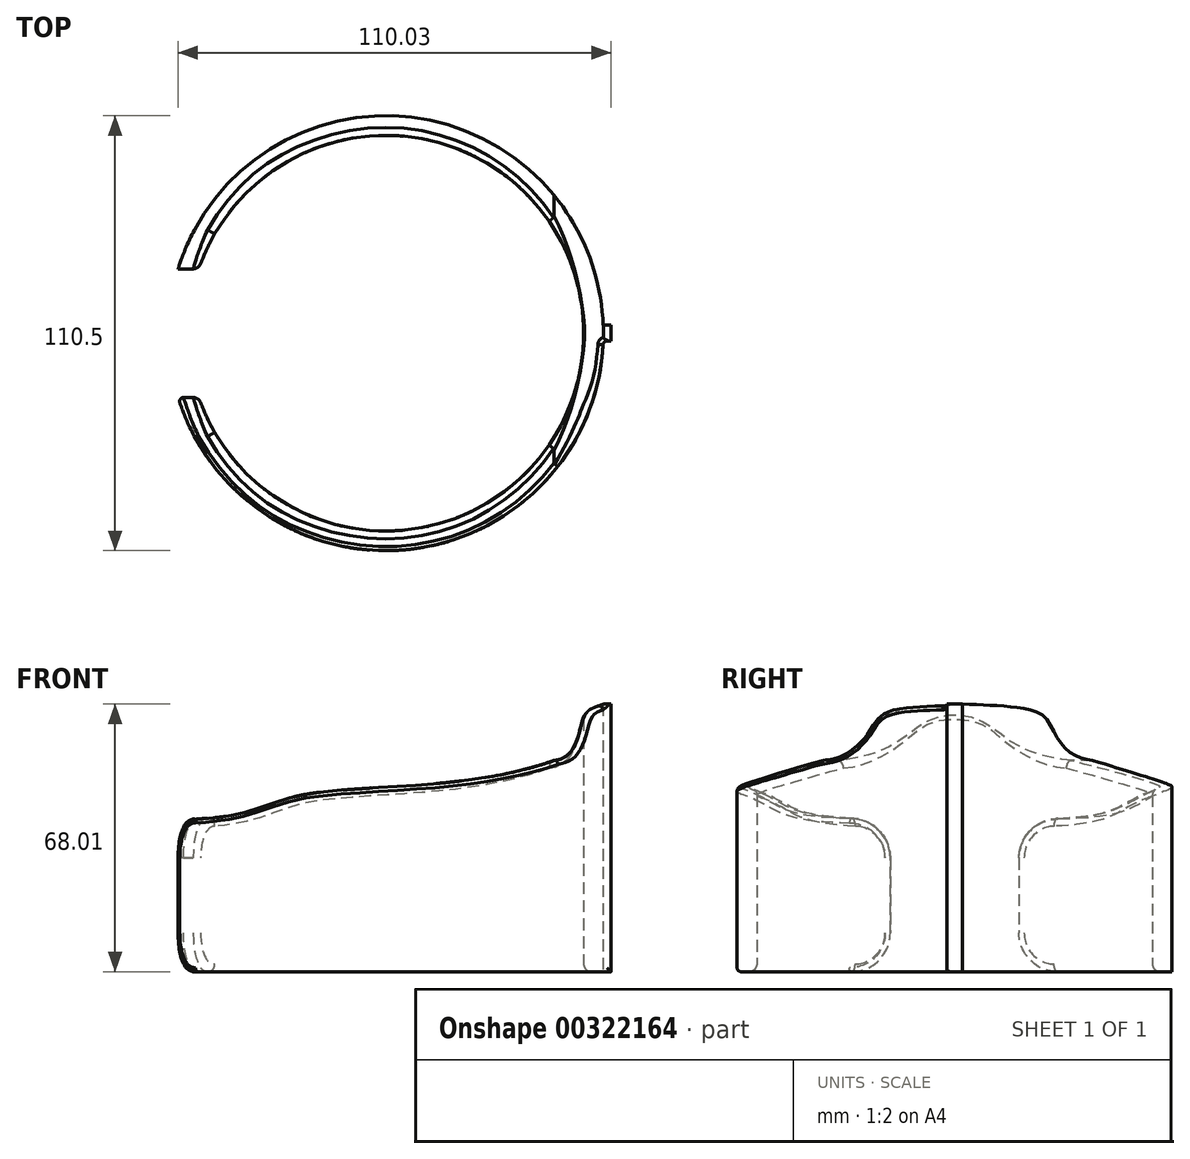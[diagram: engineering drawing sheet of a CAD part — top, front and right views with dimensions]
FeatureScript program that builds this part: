
annotation { "Feature Type Name" : "Feature", "Feature Type Description" : "" }
export const myFeature = defineFeature(function(context is Context, id is Id, definition is map)
    precondition{}
    {
        {
            var Q0;
            Q0=qCreatedBy(makeId("Top.planeOp"),FACE);
            var sketch = newSketch(context, id + "F0", { "sketchPlane" : qUnion([Q0])});
            skArc(sketch, "E0", {"start": v(-52.78, -16.35) * mm, "mid": v(7.28, -54.77) * mm, "end": v(55.21, -2) * mm});
            skArc(sketch, "E1.0", {"start": v(-47.52, -16.35) * mm, "mid": v(50.25, 0) * mm, "end": v(-47.52, 16.35) * mm});
            skLineSegment(sketch, "E2.bottom", {"start": v(-47.52, 16.35) * mm, "end": v(-52.78, 16.35) * mm});
            skLineSegment(sketch, "E2.top", {"start": v(-47.52, -16.35) * mm, "end": v(-52.78, -16.35) * mm});
            skPoint(sketch, "E2.middle", {"position": v(-55.25, 0) * mm});
            skPoint(sketch, "E2.right.start.orphan", {"position": v(-71.6, 16.35) * mm});
            skPoint(sketch, "E3.orphan", {"position": v(-71.6, -16.35) * mm});
            skPoint(sketch, "E4.orphan", {"position": v(-38.9, -16.35) * mm});
            skPoint(sketch, "E5.orphan", {"position": v(-38.9, 16.35) * mm});
            skLineSegment(sketch, "E6", {"start": v(0, 0) * mm, "end": v(55.25, 0) * mm, "construction": true});
            skPoint(sketch, "E7.end.orphan", {"position": v(57.25, 0) * mm});
            skLineSegment(sketch, "E8.bottom", {"start": v(57.25, 2) * mm, "end": v(55.21, 2) * mm});
            skLineSegment(sketch, "E8.top", {"start": v(57.25, -2) * mm, "end": v(55.21, -2) * mm});
            skLineSegment(sketch, "E8.left", {"start": v(57.25, 2) * mm, "end": v(57.25, -2) * mm});
            skPoint(sketch, "E8.middle", {"position": v(55.25, 0) * mm});
            skPoint(sketch, "E9.orphan", {"position": v(53.25, 2) * mm});
            skPoint(sketch, "E10.orphan", {"position": v(53.25, -2) * mm});
            skArc(sketch, "E11.trimOffspring", {"start": v(55.21, 2) * mm, "mid": v(7.28, 54.77) * mm, "end": v(-52.78, 16.35) * mm});
            skSolve(sketch);
        }
        {
            var Q0;
            Q0 = qSketchRegion(id + "F0", true);
            extrude(context, id + "F1", {"entities" : qUnion([Q0]), "depth" : 70 * mm});
        }
        {
            var Q0;
            Q0=qCreatedBy(makeId("Front.planeOp"),FACE);
            cPlane(context, id + "F2", {"entities" : qUnion([Q0]), "cplaneType" : CPlaneType.OFFSET, "offset" : 59 * mm, "width" : 150 * mm, "height" : 150 * mm});
        }
        {
            var Q0;
            Q0=qCreatedBy(id+"F2.planeOp",FACE);
            var sketch = newSketch(context, id + "F3", { "sketchPlane" : qUnion([Q0])});
            skFitSpline(sketch, "E12", {"points": [v(55.25, 68) * mm, v(50.35, 64.85) * mm, v(42.72, 53.7) * mm], "startDerivative": vector(-16.92, -6.6) * mm, "endDerivative": vector(-31.04, -3) * mm});
            skLineSegment(sketch, "E13", {"start": v(42.72, 53.7) * mm, "end": v(42.72, 0) * mm, "construction": true});
            skFitSpline(sketch, "E14", {"points": [v(42.72, 53.7) * mm, v(-21.35, 44.9) * mm, v(-52.78, 38.8) * mm], "startDerivative": vector(-110.2, -40.04) * mm, "endDerivative": vector(-131.82, 1.76) * mm});
            skLineSegment(sketch, "E15.0", {"start": v(-52.78, 70) * mm, "end": v(-52.78, 38.8) * mm});
            skLineSegment(sketch, "E16.0", {"start": v(-52.78, 70) * mm, "end": v(55.21, 70) * mm});
            skPoint(sketch, "E17.start.orphan", {"position": v(-52.78, 0) * mm});
            skPoint(sketch, "E18.start.orphan", {"position": v(55.25, 0) * mm});
            skLineSegment(sketch, "E19.0", {"start": v(57.25, 70) * mm, "end": v(57.25, 0) * mm});
            skLineSegment(sketch, "E20", {"start": v(55.25, 0) * mm, "end": v(55.25, 16.8) * mm});
            skLineSegment(sketch, "E21", {"start": v(55.25, 16.8) * mm, "end": v(57.25, 16.8) * mm});
            skLineSegment(sketch, "E22", {"start": v(57.25, 16.8) * mm, "end": v(57.25, 68) * mm});
            skLineSegment(sketch, "E23", {"start": v(57.25, 68) * mm, "end": v(55.25, 68) * mm});
            skLineSegment(sketch, "E24", {"start": v(55.21, 70) * mm, "end": v(57.25, 70) * mm});
            skSolve(sketch);
        }
        {
            var Q0;
            Q0=makeQuery(id+"F3.imprint","IMPRINT",FACE,{"disambiguationData":[TD([[makeQuery(id+"F3.imprint","IMPRINT",EDGE,{"derivedFrom":sQuery(id+"F3.wireOp",EDGE,"E12")}),-1.0]])]});
            extrude(context, id + "F4", {"entities" : qUnion([Q0]), "operationType" : NewBodyOperationType.REMOVE, "oppositeDirection" : true, "depth" : 127.5 * mm});
        }
        {
            var Q0;
            Q0=makeQuery(id+"F4.boolean.opBoolean","INTERSECT",EDGE,{"derivedFrom":[makeQuery(id+"F1.opExtrude","SWEPT_FACE",FACE,{"disambiguationData":[OSD([sQuery(id+"F0.wireOp",EDGE,"E2.bottom")])]}),makeQuery(id+"F4.opExtrude","SWEPT_FACE",FACE,{"disambiguationData":[OSD([sQuery(id+"F3.wireOp",EDGE,"E14")])]})]});
            var Q1;
            Q1=makeQuery(id+"F4.boolean.opBoolean","INTERSECT",EDGE,{"derivedFrom":[makeQuery(id+"F1.opExtrude","SWEPT_FACE",FACE,{"disambiguationData":[OSD([sQuery(id+"F0.wireOp",EDGE,"E2.top")])]}),makeQuery(id+"F4.opExtrude","SWEPT_FACE",FACE,{"disambiguationData":[OSD([sQuery(id+"F3.wireOp",EDGE,"E14")])]})]});
            var Q2;
            Q2=makeQuery(id+"F1.opExtrude","CAP_EDGE",EDGE,{"disambiguationData":[OSD([sQuery(id+"F0.wireOp",EDGE,"E2.bottom")])],"isStart":true});
            var Q3;
            Q3=makeQuery(id+"F1.opExtrude","CAP_EDGE",EDGE,{"disambiguationData":[OSD([sQuery(id+"F0.wireOp",EDGE,"E2.top")])],"isStart":true});
            fillet(context, id + "F5", {"entities" : qUnion([Q0, Q1, Q2, Q3]), "radius" : 9.9 * mm, "tangentPropagation" : true, "allowEdgeOverflow" : false});
        }
        {
            var Q0;
            Q0=makeQuery(id+"F1.opExtrude","SWEPT_FACE",FACE,{"disambiguationData":[OSD([sQuery(id+"F0.wireOp",EDGE,"E1.0")])]});
            fillet(context, id + "F6", {"entities" : qUnion([Q0]), "radius" : 2 * mm, "tangentPropagation" : true, "allowEdgeOverflow" : false});
        }
        {
            var Q0;
            Q0=makeQuery(id+"F1.opExtrude","SWEPT_FACE",FACE,{"disambiguationData":[OSD([sQuery(id+"F0.wireOp",EDGE,"E0")])]});
            fillet(context, id + "F7", {"entities" : qUnion([Q0]), "radius" : 1 * mm, "tangentPropagation" : true, "allowEdgeOverflow" : false});
        }
    });
